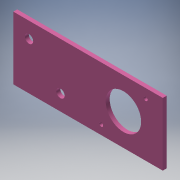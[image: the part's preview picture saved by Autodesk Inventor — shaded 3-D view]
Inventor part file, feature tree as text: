
AUTODESK INVENTOR PART (.ipt)
format: ipt  version: 2016 (Build 200138000, 138)  size: 116,224 bytes
history: native  units: in
note: dims shown in document units (in); Inventor stores cm internally (conversion verified against a paired STEP export)
features: extrude x2, sketch x2
ambient origin geometry x8: Origin, YZ Plane, XZ Plane, XY Plane, X Axis, Y Axis, Z Axis, Center Point
bodies: Solid1 (feature_tree)
feature tree (4):
  extrude  "Extrusion1"  Depth=1.0in
  extrude  "Extrusion2"  Depth=2.0in
  sketch  "Sketch1"  dims[d0=1.125in d1=1.0in]
  sketch  "Sketch2"  dims[d2=1.0in d3=2.0in d4=0.125in d5=0.125in d6=1.0in d7=1.25in d8=3.5in d9=0.7071in d10=0.7071in d11=0.125in d12=0.0in d13=0.2656in d14=0.5in d15=0.5in d16=0.2656in d17=0.5in d18=1.5in d19=0.125in d20=0.0in]
